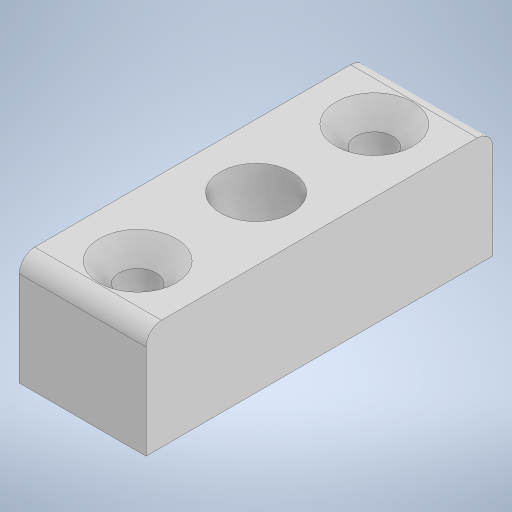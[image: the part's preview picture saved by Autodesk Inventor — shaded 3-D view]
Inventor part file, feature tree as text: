
AUTODESK INVENTOR PART (.ipt)
format: ipt  version: 2024.2 (Build 282272000, 272)  size: 382,976 bytes
history: native  units: in
note: dims shown in document units (in); Inventor stores cm internally (conversion verified against a paired STEP export)
features: extrude x2, sketch x1, fillet x1, chamfer x1
ambient origin geometry x8: Origin, YZ Plane, XZ Plane, XY Plane, X Axis, Y Axis, Z Axis, Center Point
bodies: Solid1 (feature_tree)
feature tree (5):
  sketch  "Sketch1"  dims[d0=0.325in d1=0.2875in d2=0.288in d3=0.288in d4=0.288in d5=0.17in d6=0.17in d7=0.5in d8=0.5in d9=0.25in d10=0.25in d11=0.5in d12=0.0in d21=0.15in d22=0.0in d23=0.5in d24=0.5in d25=0.156in d26=0.156in d28=0.07in d31=0.09in d32=0.125in d33=45.0deg]
  extrude  "Extrusion1"  Depth=0.07in
  extrude  "Extrusion3"  Depth=0.07in
  fillet  "Fillet5"  Radius=0.288in
  chamfer  "Chamfer2"  Distance=0.288in
